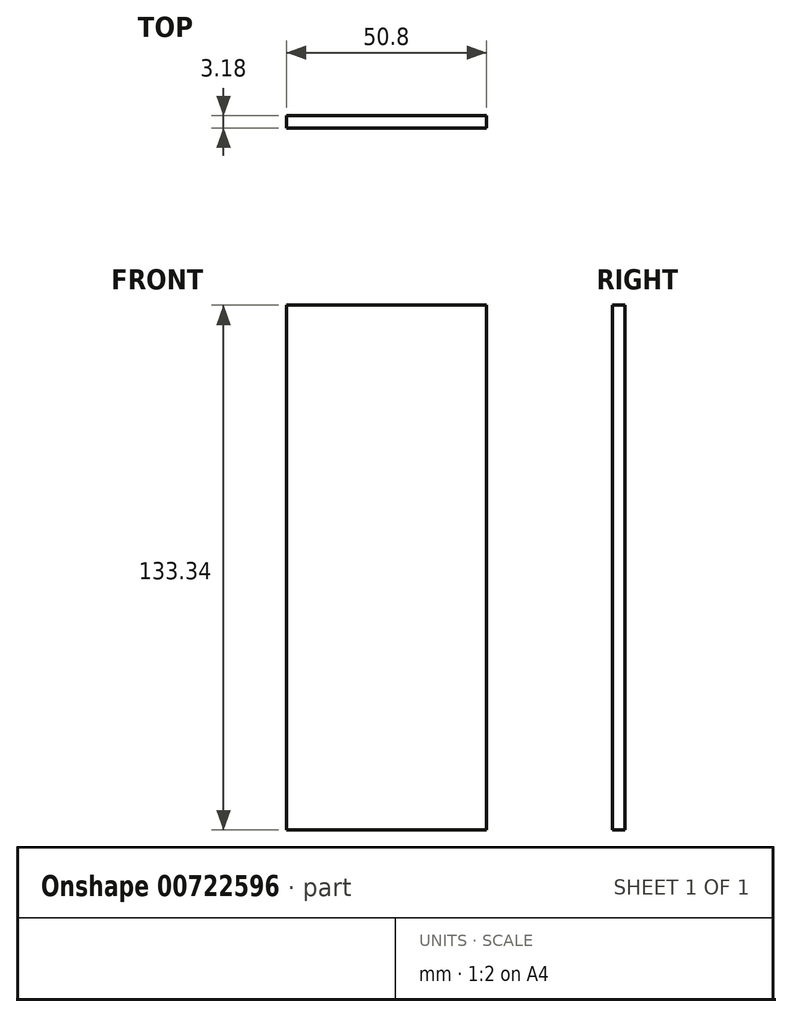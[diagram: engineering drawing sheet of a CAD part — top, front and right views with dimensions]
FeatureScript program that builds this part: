
annotation { "Feature Type Name" : "Feature", "Feature Type Description" : "" }
export const myFeature = defineFeature(function(context is Context, id is Id, definition is map)
    precondition{}
    {
        {
            var Q0;
            Q0=qCreatedBy(makeId("Front.planeOp"),FACE);
            var sketch = newSketch(context, id + "F0", { "sketchPlane" : qUnion([Q0])});
            skLineSegment(sketch, "E0.bottom", {"start": v(-25.4, -66.68) * mm, "end": v(25.4, -66.68) * mm});
            skLineSegment(sketch, "E0.top", {"start": v(-25.4, 66.68) * mm, "end": v(25.4, 66.68) * mm});
            skLineSegment(sketch, "E0.left", {"start": v(-25.4, -66.68) * mm, "end": v(-25.4, 66.68) * mm});
            skLineSegment(sketch, "E0.right", {"start": v(25.4, -66.68) * mm, "end": v(25.4, 66.68) * mm});
            skPoint(sketch, "E0.middle", {"position": v(0, 0) * mm});
            skSolve(sketch);
        }
        {
            var Q0;
            Q0=makeQuery(id+"F0.imprint","IMPRINT",FACE,{"disambiguationData":[TD([[makeQuery(id+"F0.imprint","IMPRINT",EDGE,{"derivedFrom":sQuery(id+"F0.wireOp",EDGE,"E0.bottom")}),1.0]])]});
            extrude(context, id + "F1", {"entities" : qUnion([Q0]), "endBound" : BoundingType.SYMMETRIC, "depth" : 3.17 * mm, "offsetDistance" : 25 * mm});
        }
    });
